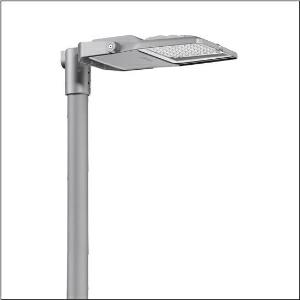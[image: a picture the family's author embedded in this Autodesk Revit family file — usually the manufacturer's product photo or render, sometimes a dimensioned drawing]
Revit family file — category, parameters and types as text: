
# Revit family: floodlight_fl_21_iq_mini___pl64_5xa7772c2e3a_d31a
name_source: partatom
category: Lighting Fixtures
units: mm (PartAtom-declared; Revit-internal decimal feet)

## family parameters
Cut with Voids When Loaded = No
Host = Face
Light Source = No
Part Type = Normal
Room Calculation Point = No
Round Connector Dimension = Use Diameter
Shared = No

## types (1)
- --- (1 x LED, 11790 lm, 87.2 W, 3000K)
    Apparent Load = 87 VA
    CIE Flux Codes = 28 80 98 100 100
    Color Rendering = 70
    Color Temperature = 3000K
    Default Elevation = 1800 mm
    Description = Floodlight FL 21 iQ mini, floodlight, primary light control with lens, of PMMA, primary optical cover: protective disc, of toughened safety glass, transparent, light distribution: PL64, light emission: direct distribution, installation type: surface-mounted, LED, High Power LED, rated luminous flux: 11.790lm, luminous efficacy: 135lm/W, light colour: 730, colour temperature: 3000K, control: Street-Remote, Auto-Match, Temp-Guard, Night-Set, Smart-Wire, optimised constant luminous flux control (CLO 2.0), Light-Fading, Lumen-Switch, with terminal, 6-pole, mains connection: 220..240V, AC, 50/60Hz, start of lifetime: 87W, end of service life: 92W, reduction: 40W, luminaire housing, of diecast aluminium, powder-coated, Siteco® metallic grey (DB 702S), corrosivity category C5 mid according to DIN EN ISO 12944, sealing non-destructively replaceable, please order mast flange separately, mast bracket, of steel, galvanised, powder-coated, protection rating (complete): IP66, insulation class (complete): insulation class II (safety insulation), certification: CE, ENEC, VDE, protection symbol: D, impact resistance: IK08, permissible operating ambient temperature: -40..+40°C, permissible operating ambient temperature for outdoor applications: -40..+50°C, standard: DIN EN 12944, LABS conformity tested according to VDMA 24364:2018-05, packaging unit: 1 piece

Light Distribution: PL64
    Height = 70 mm
    Lamp = 1 x LED
    Lamp Light Flux = 11790 lm
    Lamp Power = 87.2 W
    Lamp count = 1
    Length = 485 mm
    Luminous efficacy = 135 lm/W
    Manufacturer = Siteco
    ModVariant = No
    Model = 5XA7772C2E3A
    Number of Poles = 1
    OnlyDefault = Yes
    Power Factor = 1
    Product Name = Floodlight FL 21 iQ mini | PL64
    Product group = floodlight | pylon annexe
    ProductGroupID = 6200
    Protection Class = Protection class II
    Protection Degree = IP 66
    RLX_Detail_Level = 1
    RLX_Emergency_Light_Flux = 0 lm
    RLX_Emergency_Type = 0
    RLX_Emergency_Type_DB = No
    RlxData = <blob elided: 101137 chars, md5=ecf3c726>
    Socket = socket
    Standby Power = 0 W
    System Light Flux = 11790 lm
    System Power = 87 W
    Type Comments = factory setting: luminous flux: 100 % | dim-lin: 254 | 456 mA
    Type Image = l_1007125.jpg
    URL = http://relux.com
    VarID = @adj_136695
    Voltage = 0 V
    Weight = 0.00 kg
    Width = 337 mm

## geometry (parser evidence)
native form markers: Blend x4, Sweep x12
no freeform markers — native parametric forms only
